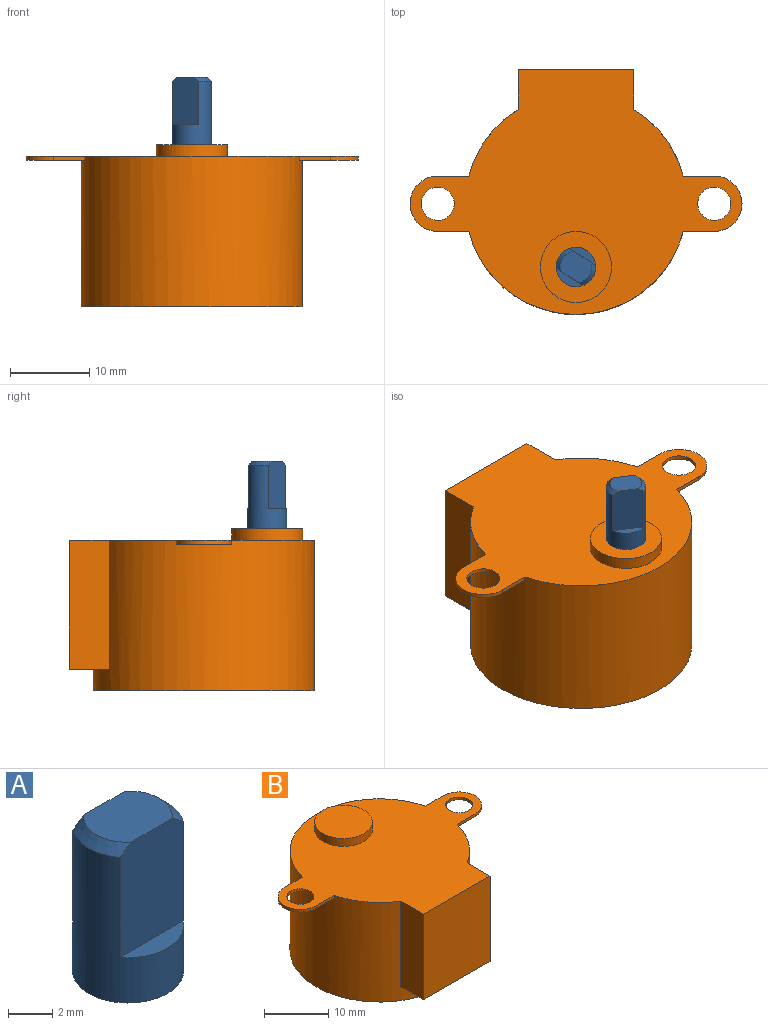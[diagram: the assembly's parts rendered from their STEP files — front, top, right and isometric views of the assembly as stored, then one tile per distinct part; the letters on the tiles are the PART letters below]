
ASSEMBLY  parts=2 mates=1
PART A: 9 faces, bbox 5x5x8.5 mm
  f0: plane 4x1mm, normal (0,0,1), area 2.8mm2, adj f2,f4
  f1: plane 4x1mm, normal (0,0,1), area 2.8mm2, adj f2,f5
  f2: cylinder r=2.5mm len=8mm, axis (0,0,-1), area 74.7mm2, adj f0,f1,f3,f4,f5,f7,f8
  f3: plane 5x5mm, normal (0,0,-1), area 19.6mm2, adj f2
  f4: plane 6x4mm, normal (0,1,0), area 23.7mm2, adj f0,f2,f6,f7,f8
  f5: plane 6x4mm, normal (0,-1,0), area 23.7mm2, adj f1,f2,f6,f7,f8
  f6: plane 4x3mm, normal (0,0,1), area 10.8mm2, adj f4,f5,f7,f8
  f7: cone r=2mm half-angle=45deg, axis (0,0,-1), area 2.3mm2, adj f2,f4,f5,f6
  f8: cone r=2mm half-angle=45deg, axis (0,0,-1), area 2.3mm2, adj f2,f4,f5,f6
PART B: 19 faces, bbox 42x31x20.5 mm
  f0: cylinder r=14mm len=28mm, axis (0,0,1), area 1413.9mm2, adj f1,f2,f7,f8,f9,f10,f11,f13
  f1: plane 28x28mm, normal (0,0,-1), area 615.8mm2, adj f0
  f2: plane 42x31mm, normal (0,0,1), area 667.5mm2, adj f0,f3,f5,f6,f8,f9,f11,f12
  f3: cylinder r=4.5mm len=9mm, axis (0,0,-1), area 42.4mm2, adj f2,f4
  f4: plane 9x9mm, normal (0,0,1), area 63.6mm2, adj f3
  f5: cylinder r=2.1mm len=4.2mm, axis (0,0,1), area 6.6mm2, adj f2,f7
  f6: cylinder r=3.5mm len=7mm, axis (0,0,1), area 5.5mm2, adj f2,f7,f8,f9
  f7: plane 7.44x7mm, normal (0,0,-1), area 30.9mm2, adj f0,f5,f6,f8,f9
  f8: plane 3.94x0.5mm, normal (0,-1,0), area 2mm2, adj f0,f2,f6,f7
  f9: plane 3.94x0.5mm, normal (0,1,0), area 2mm2, adj f0,f2,f6,f7
  f10: plane 7.44x7mm, normal (0,0,-1), area 30.9mm2, adj f0,f11,f12,f13,f14
  f11: plane 3.94x0.5mm, normal (0,1,0), area 2mm2, adj f0,f2,f10,f12
  f12: cylinder r=3.5mm len=7mm, axis (0,0,1), area 5.5mm2, adj f2,f10,f11,f13
  f13: plane 3.94x0.5mm, normal (0,-1,0), area 2mm2, adj f0,f2,f10,f12
  f14: cylinder r=2.1mm len=4.2mm, axis (0,0,1), area 6.6mm2, adj f2,f10
  f15: plane 14.6x5.05mm, normal (0,0,-1), area 53.5mm2, adj f0,f16,f17,f18
  f16: plane 16.3x5.05mm, normal (1,0,0), area 82.4mm2, adj f0,f2,f15,f18
  f17: plane 16.3x5.05mm, normal (-1,0,0), area 82.4mm2, adj f0,f2,f15,f18
  f18: plane 16.3x14.6mm, normal (0,-1,0), area 238mm2, adj f2,f15,f16,f17
PLACE A rot(axis=(0,0,1),147.1deg) t=(5.01,23.75,27.28)mm
PLACE B rot(axis=(0,0,-1),180deg) t=(5.01,31.75,25.78)mm fixed
MATE revolute B.f3 <-> A.f2  axis (0,0,1) through (5.01,23.75,27.28)mm
